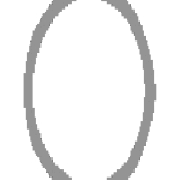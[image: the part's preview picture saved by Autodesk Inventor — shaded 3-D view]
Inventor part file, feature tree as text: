
AUTODESK INVENTOR PART (.ipt)
format: ipt  version: 2021 (Build 250183000, 183)  size: 109,056 bytes
history: native  units: in
note: dims shown in document units (in); Inventor stores cm internally (conversion verified against a paired STEP export)
features: other x4, sketch x3, plane x1
ambient origin geometry x8: Origin, YZ Plane, XZ Plane, XY Plane, X Axis, Y Axis, Z Axis, Center Point
bodies: Solid1 (feature_tree), Body (feature_tree)
feature tree (8):
  other  "Driven Length"
  other  "Frame Generator"
  other  "Start Plane"
  other  "End Plane"
  sketch  "Sketch"  dims[d2=20.6216in d4=-0.0in d5=20.6216in d6=0.12in d7=0.0in d8=90.0deg d9=20.6216in]
  sketch  "Sketch2"  dims[d0=1.0in]
  plane  "Work Plane3"
  sketch  "Sketch3"  dims[d1=0.065in]
